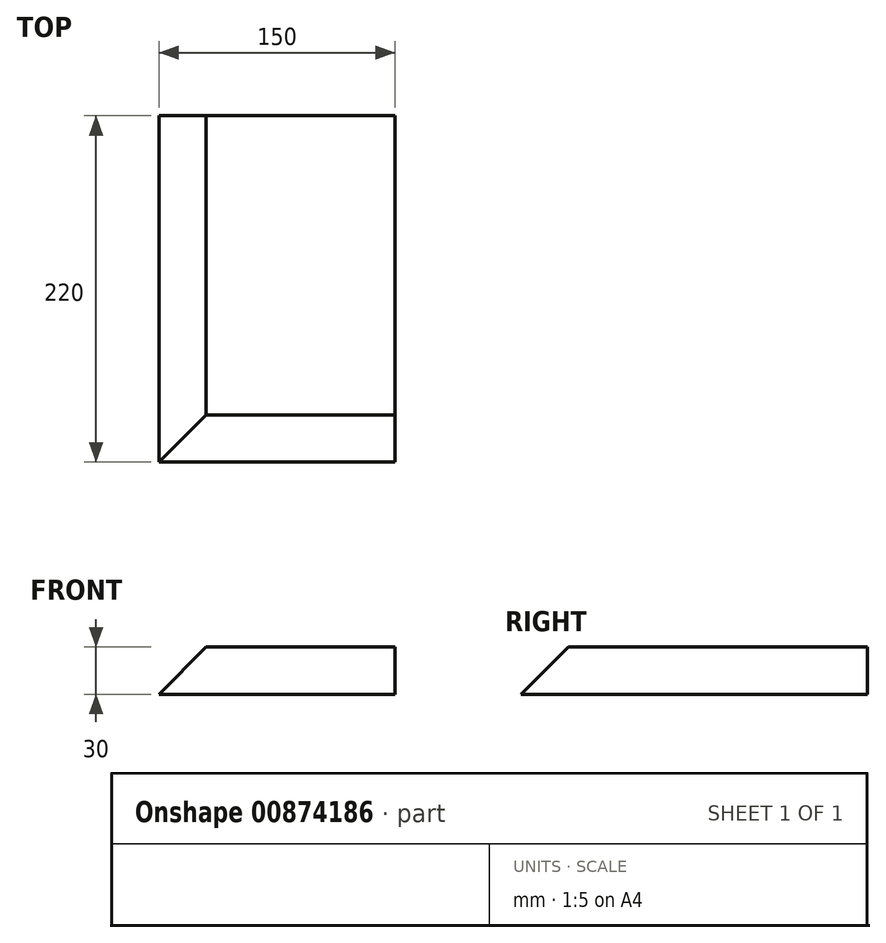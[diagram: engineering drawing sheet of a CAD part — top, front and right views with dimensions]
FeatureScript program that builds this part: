
annotation { "Feature Type Name" : "Feature", "Feature Type Description" : "" }
export const myFeature = defineFeature(function(context is Context, id is Id, definition is map)
    precondition{}
    {
        {
            var Q0;
            Q0=qCreatedBy(makeId("Top.planeOp"),FACE);
            var sketch = newSketch(context, id + "F0", { "sketchPlane" : qUnion([Q0])});
            skLineSegment(sketch, "E0.bottom", {"start": v(-70.57, 110) * mm, "end": v(79.43, 110) * mm});
            skLineSegment(sketch, "E0.top", {"start": v(-70.57, -110) * mm, "end": v(79.43, -110) * mm});
            skLineSegment(sketch, "E0.left", {"start": v(-70.57, 110) * mm, "end": v(-70.57, -110) * mm});
            skLineSegment(sketch, "E0.right", {"start": v(79.43, 110) * mm, "end": v(79.43, -110) * mm});
            skPoint(sketch, "E0.middle", {"position": v(4.43, 0) * mm});
            skSolve(sketch);
        }
        {
            var Q0;
            Q0=makeQuery(id+"F0.imprint","IMPRINT",FACE,{"disambiguationData":[TD([[makeQuery(id+"F0.imprint","IMPRINT",EDGE,{"derivedFrom":sQuery(id+"F0.wireOp",EDGE,"E0.bottom")}),-1.0]])]});
            extrude(context, id + "F1", {"entities" : qUnion([Q0]), "depth" : 30 * mm, "offsetDistance" : 25 * mm});
        }
        {
            var Q0;
            Q0=makeQuery(id+"F1.opExtrude","CAP_EDGE",EDGE,{"disambiguationData":[OSD([sQuery(id+"F0.wireOp",EDGE,"E0.top")])],"isStart":false});
            var Q1;
            Q1=makeQuery(id+"F1.opExtrude","CAP_EDGE",EDGE,{"disambiguationData":[OSD([sQuery(id+"F0.wireOp",EDGE,"E0.left")])],"isStart":false});
            chamfer(context, id + "F2", {"entities" : qUnion([Q0, Q1]), "width" : 30 * mm, "tangentPropagation" : true});
        }
    });
